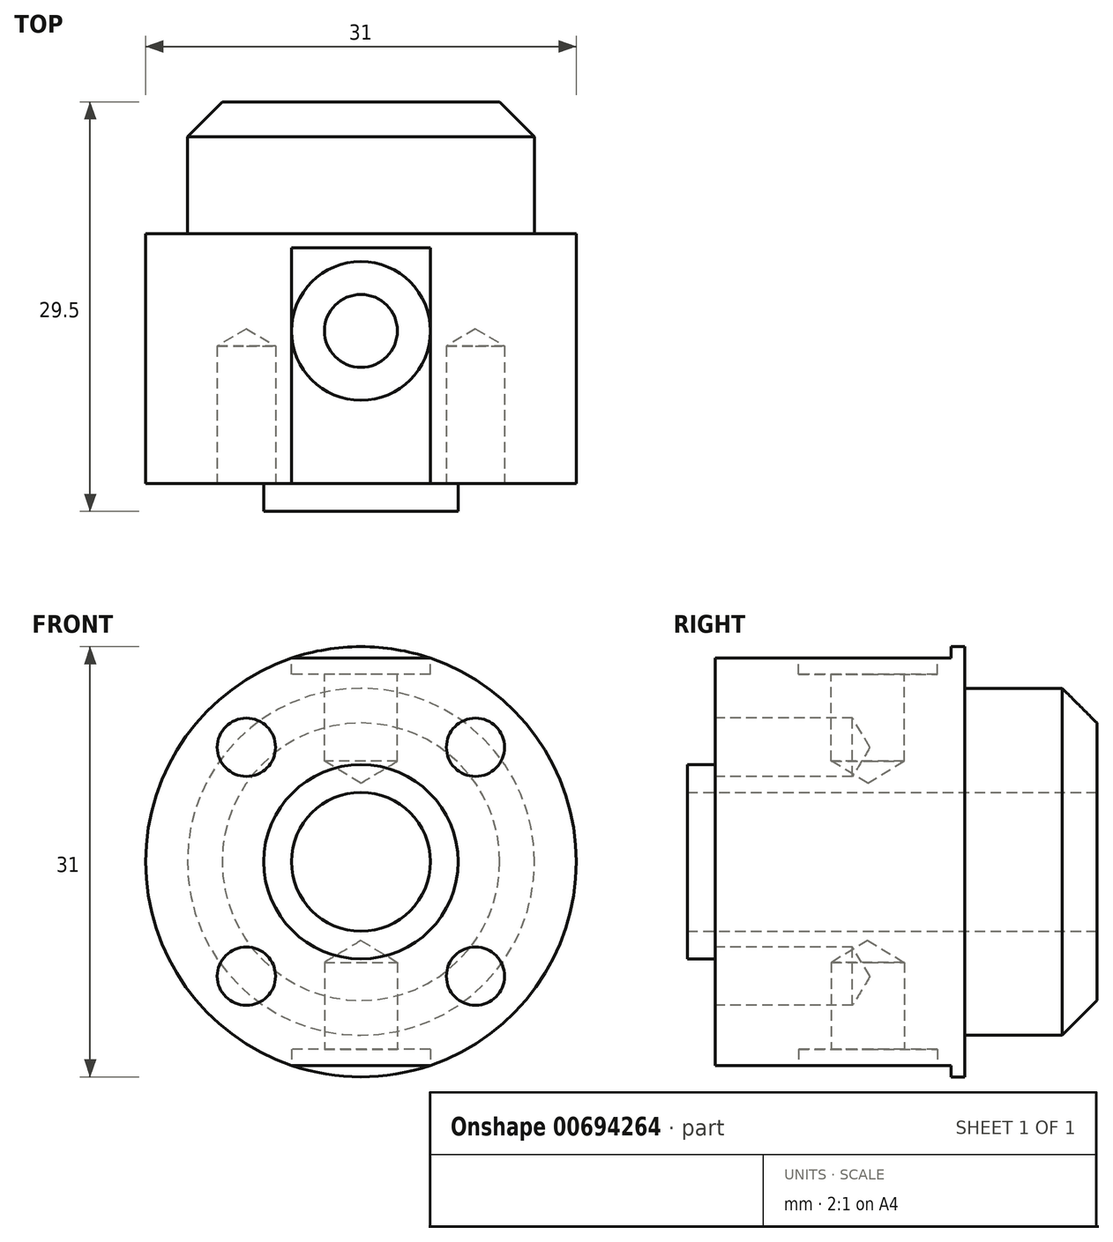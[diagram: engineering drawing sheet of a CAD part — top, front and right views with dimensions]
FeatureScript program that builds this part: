
annotation { "Feature Type Name" : "Feature", "Feature Type Description" : "" }
export const myFeature = defineFeature(function(context is Context, id is Id, definition is map)
    precondition{}
    {
        {
            var Q0;
            Q0=qCreatedBy(makeId("Right.planeOp"),FACE);
            var sketch = newSketch(context, id + "F0", { "sketchPlane" : qUnion([Q0])});
            skLineSegment(sketch, "E0", {"start": v(0, 5) * mm, "end": v(0, 15.5) * mm});
            skLineSegment(sketch, "E1", {"start": v(0, 15.5) * mm, "end": v(-18, 15.5) * mm});
            skLineSegment(sketch, "E2", {"start": v(-18, 15.5) * mm, "end": v(-18, 7) * mm});
            skLineSegment(sketch, "E3", {"start": v(-18, 7) * mm, "end": v(-20, 7) * mm});
            skLineSegment(sketch, "E4", {"start": v(-20, 7) * mm, "end": v(-20, 5) * mm});
            skPoint(sketch, "E5.startSnap0", {"position": v(0, 7.75) * mm});
            skLineSegment(sketch, "E6", {"start": v(0, 5) * mm, "end": v(-20, 5) * mm});
            skPoint(sketch, "E7.end.orphan", {"position": v(0, 0) * mm});
            skPoint(sketch, "E8.orphan", {"position": v(-20, 0) * mm});
            skLineSegment(sketch, "E9", {"start": v(0, 0) * mm, "end": v(-26.18, 0) * mm, "construction": true});
            skSolve(sketch);
        }
        {
            var Q0;
            Q0=qSketchRegion(id+"F0",true);
            var Q1;
            Q1=sQuery(id+"F0.wireOp",EDGE,"E9");
            revolve(context, id + "F1", {"entities" : qUnion([Q0]), "axis" : qUnion([Q1]), "revolveType" : RevolveType.FULL});
        }
        {
            var Q0;
            Q0=makeQuery(id+"F1.opRevolve","SWEPT_FACE",FACE,{"disambiguationData":[OSD([sQuery(id+"F0.wireOp",EDGE,"E2")])]});
            var sketch = newSketch(context, id + "F2", { "sketchPlane" : qUnion([Q0])});
            skCircle(sketch, "E10", {"center": v(8.25, 8.25) * mm, "radius": 1.5 * mm});
            skCircle(sketch, "E11.1.0", {"center": v(-8.25, 8.25) * mm, "radius": 1.5 * mm});
            skCircle(sketch, "E11.2.0", {"center": v(-8.25, -8.25) * mm, "radius": 1.5 * mm});
            skCircle(sketch, "E11.3.0", {"center": v(8.25, -8.25) * mm, "radius": 1.5 * mm});
            skPoint(sketch, "E11.center", {"position": v(0, 0) * mm});
            skSolve(sketch);
        }
        {
            var Q0;
            Q0=qSketchRegion(id+"F2",true);
            extrude(context, id + "F3", {"entities" : qUnion([Q0]), "operationType" : NewBodyOperationType.REMOVE, "oppositeDirection" : true, "depth" : 7.5 * mm, "offsetDistance" : 25 * mm});
        }
        {
            var Q0;
            Q0=makeQuery(id+"F1.opRevolve","SWEPT_FACE",FACE,{"disambiguationData":[OSD([sQuery(id+"F0.wireOp",EDGE,"E2")])]});
            var sketch = newSketch(context, id + "F4", { "sketchPlane" : qUnion([Q0])});
            skCircle(sketch, "E12", {"center": v(8.25, 8.25) * mm, "radius": 1.53 * mm});
            skCircle(sketch, "E13.1.0", {"center": v(-8.25, 8.25) * mm, "radius": 1.53 * mm});
            skCircle(sketch, "E13.2.0", {"center": v(-8.25, -8.25) * mm, "radius": 1.53 * mm});
            skCircle(sketch, "E13.3.0", {"center": v(8.25, -8.25) * mm, "radius": 1.53 * mm});
            skPoint(sketch, "E13.center", {"position": v(0, 0) * mm});
            skSolve(sketch);
        }
        {
            var Q0;
            Q0=sQuery(id+"F4.wireOp",VERTEX,"E12.center");
            var Q1;
            Q1=sQuery(id+"F4.wireOp",VERTEX,"E13.1.0.center");
            var Q2;
            Q2=sQuery(id+"F4.wireOp",VERTEX,"E13.2.0.center");
            var Q3;
            Q3=sQuery(id+"F4.wireOp",VERTEX,"E13.3.0.center");
            var Q4;
            Q4=makeQuery(id+"F1.opRevolve","SWEPT_BODY",BODY,{"disambiguationData":[OSD([sQuery(id+"F0.wireOp",EDGE,"E0"),sQuery(id+"F0.wireOp",EDGE,"E1"),sQuery(id+"F0.wireOp",EDGE,"E2"),sQuery(id+"F0.wireOp",EDGE,"E3"),sQuery(id+"F0.wireOp",EDGE,"E4"),sQuery(id+"F0.wireOp",EDGE,"E6")])]});
            hole(context, id + "F5", {"style" : HoleStyle.SIMPLE, "endStyle" : HoleEndStyle.BLIND, "standardTappedOrClearance" : lookupTablePath({ "standard" : "ISO", "engagement" : "75%", "pitch" : "0.8 mm", "size" : "M5", "type" : "Tapped" }), "standardBlindInLast" : lookupTablePath({ "standard" : "ISO", "engagement" : "75%", "pitch" : "0.8 mm", "size" : "M5", "type" : "Tapped" }), "holeDiameter" : 4.2 * mm, "majorDiameter" : 5 * mm, "showTappedDepth" : true, "holeDepth" : 9.9 * mm, "isTappedThrough" : true, "tappedDepth" : 7.5 * mm, "tapClearance" : 3, "locations" : qUnion([Q0, Q1, Q2, Q3]), "scope" : qUnion([Q4])});
        }
        {
            var Q0;
            Q0=qCreatedBy(makeId("Top.planeOp"),FACE);
            cPlane(context, id + "F6", {"entities" : qUnion([Q0]), "cplaneType" : CPlaneType.OFFSET, "offset" : 15.5 * mm, "width" : 150 * mm, "height" : 150 * mm});
        }
        {
            var Q0;
            Q0=qCreatedBy(id+"F6.planeOp",FACE);
            var sketch = newSketch(context, id + "F7", { "sketchPlane" : qUnion([Q0])});
            skCircle(sketch, "E14", {"center": v(0, -7) * mm, "radius": 5 * mm});
            skSolve(sketch);
        }
        {
            var Q0;
            Q0=qSketchRegion(id+"F7",true);
            extrude(context, id + "F8", {"entities" : qUnion([Q0]), "operationType" : NewBodyOperationType.REMOVE, "oppositeDirection" : true, "depth" : 2 * mm, "offsetDistance" : 25 * mm});
        }
        {
            var Q0;
            Q0=qCreatedBy(id+"F6.planeOp",FACE);
            var sketch = newSketch(context, id + "F9", { "sketchPlane" : qUnion([Q0])});
            skCircle(sketch, "E15", {"center": v(0, -7) * mm, "radius": 2.69 * mm});
            skSolve(sketch);
        }
        {
            var Q0;
            Q0=sQuery(id+"F9.wireOp",VERTEX,"E15.center");
            var Q1;
            Q1=makeQuery(id+"F1.opRevolve","SWEPT_BODY",BODY,{"disambiguationData":[OSD([sQuery(id+"F0.wireOp",EDGE,"E0"),sQuery(id+"F0.wireOp",EDGE,"E1"),sQuery(id+"F0.wireOp",EDGE,"E2"),sQuery(id+"F0.wireOp",EDGE,"E3"),sQuery(id+"F0.wireOp",EDGE,"E4"),sQuery(id+"F0.wireOp",EDGE,"E6")])]});
            hole(context, id + "F10", {"style" : HoleStyle.SIMPLE, "endStyle" : HoleEndStyle.BLIND, "standardTappedOrClearance" : lookupTablePath({ "standard" : "ISO", "engagement" : "75%", "pitch" : "0.75 mm", "size" : "M6", "type" : "Tapped" }), "standardBlindInLast" : lookupTablePath({ "standard" : "ISO", "engagement" : "75%", "pitch" : "0.75 mm", "size" : "M6", "type" : "Tapped" }), "holeDiameter" : 5.25 * mm, "majorDiameter" : 6 * mm, "showTappedDepth" : true, "holeDepth" : 6.25 * mm, "isTappedThrough" : true, "tappedDepth" : 6.25 * mm, "tapClearance" : 0, "locations" : qUnion([Q0]), "scope" : qUnion([Q1])});
        }
        {
            var Q0;
            Q0=qCreatedBy(makeId("Top.planeOp"),FACE);
            cPlane(context, id + "F11", {"entities" : qUnion([Q0]), "cplaneType" : CPlaneType.OFFSET, "offset" : 15.5 * mm, "oppositeDirection" : true, "width" : 150 * mm, "height" : 150 * mm});
        }
        {
            var Q0;
            Q0=qCreatedBy(id+"F11.planeOp",FACE);
            var sketch = newSketch(context, id + "F12", { "sketchPlane" : qUnion([Q0])});
            skCircle(sketch, "E16", {"center": v(0, -7) * mm, "radius": 5 * mm});
            skSolve(sketch);
        }
        {
            var Q0;
            Q0=qSketchRegion(id+"F12",true);
            extrude(context, id + "F13", {"entities" : qUnion([Q0]), "operationType" : NewBodyOperationType.REMOVE, "depth" : 2 * mm, "offsetDistance" : 25 * mm});
        }
        {
            var Q0;
            Q0=makeQuery(id+"F13.boolean.opBoolean","COPY",FACE,{"derivedFrom":makeQuery(id+"F13.opExtrude","CAP_FACE",FACE,{"disambiguationData":[OSD([sQuery(id+"F12.wireOp",EDGE,"E16")])],"isStart":false})});
            var sketch = newSketch(context, id + "F14", { "sketchPlane" : qUnion([Q0])});
            skCircle(sketch, "E17", {"center": v(0, 7) * mm, "radius": 2.26 * mm});
            skSolve(sketch);
        }
        {
            var Q0;
            Q0=sQuery(id+"F14.wireOp",VERTEX,"E17.center");
            var Q1;
            Q1=makeQuery(id+"F1.opRevolve","SWEPT_BODY",BODY,{"disambiguationData":[OSD([sQuery(id+"F0.wireOp",EDGE,"E0"),sQuery(id+"F0.wireOp",EDGE,"E1"),sQuery(id+"F0.wireOp",EDGE,"E2"),sQuery(id+"F0.wireOp",EDGE,"E3"),sQuery(id+"F0.wireOp",EDGE,"E4"),sQuery(id+"F0.wireOp",EDGE,"E6")])]});
            hole(context, id + "F15", {"style" : HoleStyle.SIMPLE, "endStyle" : HoleEndStyle.BLIND, "standardTappedOrClearance" : lookupTablePath({ "standard" : "ISO", "engagement" : "75%", "pitch" : "0.75 mm", "size" : "M6", "type" : "Tapped" }), "standardBlindInLast" : lookupTablePath({ "standard" : "ISO", "engagement" : "75%", "pitch" : "0.75 mm", "size" : "M6", "type" : "Tapped" }), "holeDiameter" : 5.25 * mm, "majorDiameter" : 6 * mm, "showTappedDepth" : true, "holeDepth" : 6.25 * mm, "isTappedThrough" : true, "tappedDepth" : 6.25 * mm, "tapClearance" : 0, "locations" : qUnion([Q0]), "scope" : qUnion([Q1])});
        }
        {
            var Q0;
            Q0=makeQuery(id+"F1.opRevolve","SWEPT_FACE",FACE,{"disambiguationData":[OSD([sQuery(id+"F0.wireOp",EDGE,"E0")])]});
            var sketch = newSketch(context, id + "F16", { "sketchPlane" : qUnion([Q0])});
            skCircle(sketch, "E18", {"center": v(0, 0) * mm, "radius": 12.5 * mm});
            skCircle(sketch, "E19", {"center": v(0, 0) * mm, "radius": 5 * mm});
            skSolve(sketch);
        }
        {
            var Q0;
            Q0=qSketchRegion(id+"F16",true);
            extrude(context, id + "F17", {"entities" : qUnion([Q0]), "operationType" : NewBodyOperationType.ADD, "depth" : 9.5 * mm, "offsetDistance" : 25 * mm});
        }
        {
            var Q0;
            Q0=makeQuery(id+"F17.opExtrude","CAP_EDGE",EDGE,{"disambiguationData":[OSD([sQuery(id+"F16.wireOp",EDGE,"E18")])],"isStart":false});
            chamfer(context, id + "F18", {"entities" : qUnion([Q0]), "width" : 2.5 * mm, "tangentPropagation" : true});
        }
        {
            var Q0;
            Q0=makeQuery(id+"F1.opRevolve","SWEPT_FACE",FACE,{"disambiguationData":[OSD([sQuery(id+"F0.wireOp",EDGE,"E2")])]});
            var sketch = newSketch(context, id + "F19", { "sketchPlane" : qUnion([Q0])});
            skArc(sketch, "E20", {"start": v(5, 14.67) * mm, "mid": v(0, 15.5) * mm, "end": v(-5, 14.67) * mm});
            skLineSegment(sketch, "E21", {"start": v(5, -14.67) * mm, "end": v(-5, -14.67) * mm});
            skLineSegment(sketch, "E22", {"start": v(5, 14.67) * mm, "end": v(-5, 14.67) * mm});
            skArc(sketch, "E23.trimOffspring", {"start": v(-5, -14.67) * mm, "mid": v(0, -15.5) * mm, "end": v(5, -14.67) * mm});
            skSolve(sketch);
        }
        {
            var Q0;
            Q0=qSketchRegion(id+"F19",true);
            extrude(context, id + "F20", {"entities" : qUnion([Q0]), "operationType" : NewBodyOperationType.REMOVE, "oppositeDirection" : true, "depth" : 17 * mm, "offsetDistance" : 25 * mm});
        }
    });
